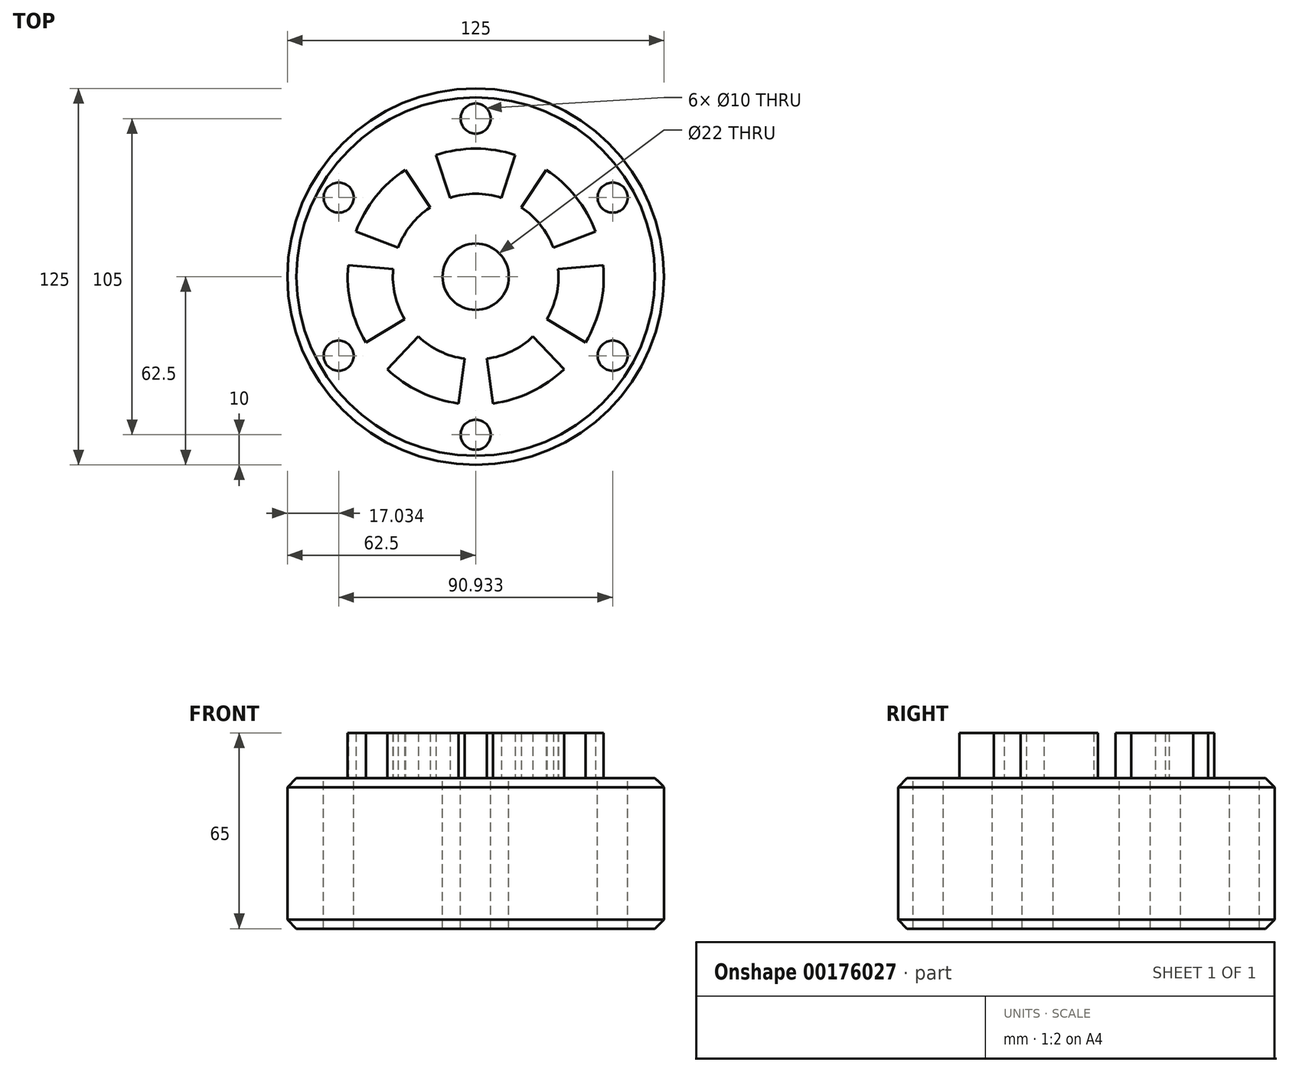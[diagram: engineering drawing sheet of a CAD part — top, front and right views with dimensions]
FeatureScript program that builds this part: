
annotation { "Feature Type Name" : "Feature", "Feature Type Description" : "" }
export const myFeature = defineFeature(function(context is Context, id is Id, definition is map)
    precondition{}
    {
        {
            var Q0;
            Q0=qCreatedBy(makeId("Top.planeOp"),FACE);
            var sketch = newSketch(context, id + "F0", { "sketchPlane" : qUnion([Q0])});
            skCircle(sketch, "E0", {"center": v(0, 0) * mm, "radius": 62.5 * mm});
            skSolve(sketch);
        }
        {
            var Q0;
            Q0=makeQuery(id+"F0.imprint","IMPRINT",FACE,{"disambiguationData":[TD([[makeQuery(id+"F0.imprint","IMPRINT",EDGE,{"derivedFrom":sQuery(id+"F0.wireOp",EDGE,"E0")}),1.0]])]});
            extrude(context, id + "F1", {"entities" : qUnion([Q0]), "depth" : 50 * mm});
        }
        {
            var Q0;
            Q0=makeQuery(id+"F1.opExtrude","CAP_FACE",FACE,{"disambiguationData":[OSD([sQuery(id+"F0.wireOp",EDGE,"E0")])],"isStart":false});
            var sketch = newSketch(context, id + "F2", { "sketchPlane" : qUnion([Q0])});
            skArc(sketch, "E1", {"start": v(8.5, 26.15) * mm, "mid": v(0, 27.5) * mm, "end": v(-8.5, 26.15) * mm});
            skArc(sketch, "E2", {"start": v(13.14, 40.42) * mm, "mid": v(0, 42.5) * mm, "end": v(-13.14, 40.42) * mm});
            skLineSegment(sketch, "E3", {"start": v(-8.5, 26.15) * mm, "end": v(-13.14, 40.42) * mm});
            skLineSegment(sketch, "E4", {"start": v(8.5, 26.15) * mm, "end": v(13.14, 40.42) * mm});
            skLineSegment(sketch, "E5.1.0", {"start": v(-25.75, 9.66) * mm, "end": v(-39.8, 14.93) * mm});
            skArc(sketch, "E5.1.1", {"start": v(-23.41, 35.47) * mm, "mid": v(-33.23, 26.5) * mm, "end": v(-39.8, 14.93) * mm});
            skLineSegment(sketch, "E5.1.2", {"start": v(-15.15, 22.95) * mm, "end": v(-23.41, 35.47) * mm});
            skArc(sketch, "E5.1.3", {"start": v(-15.15, 22.95) * mm, "mid": v(-21.5, 17.15) * mm, "end": v(-25.75, 9.66) * mm});
            skLineSegment(sketch, "E5.2.0", {"start": v(-23.6, -14.1) * mm, "end": v(-36.48, -21.8) * mm});
            skArc(sketch, "E5.2.1", {"start": v(-42.33, 3.81) * mm, "mid": v(-41.43, -9.46) * mm, "end": v(-36.48, -21.8) * mm});
            skLineSegment(sketch, "E5.2.2", {"start": v(-27.39, 2.47) * mm, "end": v(-42.33, 3.81) * mm});
            skArc(sketch, "E5.2.3", {"start": v(-27.39, 2.47) * mm, "mid": v(-26.81, -6.12) * mm, "end": v(-23.6, -14.1) * mm});
            skLineSegment(sketch, "E5.3.0", {"start": v(-3.69, -27.25) * mm, "end": v(-5.7, -42.12) * mm});
            skArc(sketch, "E5.3.1", {"start": v(-29.37, -30.72) * mm, "mid": v(-18.44, -38.3) * mm, "end": v(-5.7, -42.12) * mm});
            skLineSegment(sketch, "E5.3.2", {"start": v(-19, -19.88) * mm, "end": v(-29.37, -30.72) * mm});
            skArc(sketch, "E5.3.3", {"start": v(-19, -19.88) * mm, "mid": v(-11.93, -24.78) * mm, "end": v(-3.69, -27.25) * mm});
            skLineSegment(sketch, "E5.4.0", {"start": v(19, -19.88) * mm, "end": v(29.37, -30.72) * mm});
            skArc(sketch, "E5.4.1", {"start": v(5.7, -42.12) * mm, "mid": v(18.44, -38.3) * mm, "end": v(29.37, -30.72) * mm});
            skLineSegment(sketch, "E5.4.2", {"start": v(3.69, -27.25) * mm, "end": v(5.7, -42.12) * mm});
            skArc(sketch, "E5.4.3", {"start": v(3.69, -27.25) * mm, "mid": v(11.93, -24.78) * mm, "end": v(19, -19.88) * mm});
            skLineSegment(sketch, "E5.5.0", {"start": v(27.39, 2.47) * mm, "end": v(42.33, 3.81) * mm});
            skArc(sketch, "E5.5.1", {"start": v(36.48, -21.8) * mm, "mid": v(41.43, -9.46) * mm, "end": v(42.33, 3.81) * mm});
            skLineSegment(sketch, "E5.5.2", {"start": v(23.6, -14.1) * mm, "end": v(36.48, -21.8) * mm});
            skArc(sketch, "E5.5.3", {"start": v(23.6, -14.1) * mm, "mid": v(26.81, -6.12) * mm, "end": v(27.39, 2.47) * mm});
            skLineSegment(sketch, "E5.6.0", {"start": v(15.15, 22.95) * mm, "end": v(23.41, 35.47) * mm});
            skArc(sketch, "E5.6.1", {"start": v(39.8, 14.93) * mm, "mid": v(33.23, 26.5) * mm, "end": v(23.41, 35.47) * mm});
            skLineSegment(sketch, "E5.6.2", {"start": v(25.75, 9.66) * mm, "end": v(39.8, 14.93) * mm});
            skArc(sketch, "E5.6.3", {"start": v(25.75, 9.66) * mm, "mid": v(21.5, 17.15) * mm, "end": v(15.15, 22.95) * mm});
            skSolve(sketch);
        }
        {
            var Q0;
            Q0 = qSketchRegion(id + "F2", true);
            extrude(context, id + "F3", {"entities" : qUnion([Q0]), "operationType" : NewBodyOperationType.ADD, "depth" : 15 * mm});
        }
        {
            var Q0;
            Q0=makeQuery(id+"F1.opExtrude","CAP_FACE",FACE,{"disambiguationData":[OSD([sQuery(id+"F0.wireOp",EDGE,"E0")])],"isStart":false});
            var sketch = newSketch(context, id + "F4", { "sketchPlane" : qUnion([Q0])});
            skCircle(sketch, "E6", {"center": v(0, 0) * mm, "radius": 11 * mm});
            skSolve(sketch);
        }
        {
            var Q0;
            Q0 = qSketchRegion(id + "F4", true);
            extrude(context, id + "F5", {"entities" : qUnion([Q0]), "operationType" : NewBodyOperationType.REMOVE, "endBound" : BoundingType.THROUGH_ALL, "oppositeDirection" : true, "depth" : 25 * mm});
        }
        {
            var Q0;
            Q0=makeQuery(id+"F1.opExtrude","CAP_FACE",FACE,{"disambiguationData":[OSD([sQuery(id+"F0.wireOp",EDGE,"E0")])],"isStart":false});
            var sketch = newSketch(context, id + "F6", { "sketchPlane" : qUnion([Q0])});
            skArc(sketch, "E7", {"start": v(-42.76, 30.46) * mm, "mid": v(-44.16, 28.39) * mm, "end": v(-45.47, 26.25) * mm});
            skCircle(sketch, "E8", {"center": v(0, 52.5) * mm, "radius": 5 * mm});
            skCircle(sketch, "E9.1.0", {"center": v(-45.47, 26.25) * mm, "radius": 5 * mm});
            skArc(sketch, "E9.1.1", {"start": v(-42.76, 30.46) * mm, "mid": v(-45.47, 26.25) * mm, "end": v(-47.76, 21.8) * mm});
            skCircle(sketch, "E9.2.0", {"center": v(-45.47, -26.25) * mm, "radius": 5 * mm});
            skCircle(sketch, "E9.3.0", {"center": v(0, -52.5) * mm, "radius": 5 * mm});
            skArc(sketch, "E9.3.1", {"start": v(-42.76, 30.46) * mm, "mid": v(-45.47, 26.25) * mm, "end": v(-47.76, 21.8) * mm});
            skCircle(sketch, "E9.4.0", {"center": v(45.47, -26.25) * mm, "radius": 5 * mm});
            skArc(sketch, "E9.4.1", {"start": v(-42.76, 30.46) * mm, "mid": v(-45.47, 26.25) * mm, "end": v(-47.76, 21.8) * mm});
            skCircle(sketch, "E9.5.0", {"center": v(45.47, 26.25) * mm, "radius": 5 * mm});
            skArc(sketch, "E9.5.1", {"start": v(-42.76, 30.46) * mm, "mid": v(-45.47, 26.25) * mm, "end": v(-47.76, 21.8) * mm});
            skArc(sketch, "E10.trimOffspring", {"start": v(5, 52.26) * mm, "mid": v(0, 52.5) * mm, "end": v(-5, 52.26) * mm});
            skArc(sketch, "E11.trimOffspring", {"start": v(47.76, 21.8) * mm, "mid": v(45.47, 26.25) * mm, "end": v(42.76, 30.46) * mm});
            skArc(sketch, "E12.trimOffspring", {"start": v(47.76, 21.8) * mm, "mid": v(46.66, 24.06) * mm, "end": v(45.47, 26.25) * mm});
            skArc(sketch, "E13.trimOffspring", {"start": v(42.76, -30.46) * mm, "mid": v(45.47, -26.25) * mm, "end": v(47.76, -21.8) * mm});
            skArc(sketch, "E14.trimOffspring", {"start": v(-5, -52.26) * mm, "mid": v(0, -52.5) * mm, "end": v(5, -52.26) * mm});
            skArc(sketch, "E15.trimOffspring", {"start": v(-5, -52.26) * mm, "mid": v(-2.5, -52.44) * mm, "end": v(0, -52.5) * mm});
            skArc(sketch, "E16.trimOffspring", {"start": v(-47.76, -21.8) * mm, "mid": v(-45.47, -26.25) * mm, "end": v(-42.76, -30.46) * mm});
            skArc(sketch, "E17.trimOffspring", {"start": v(-47.76, -21.8) * mm, "mid": v(-46.66, -24.06) * mm, "end": v(-45.47, -26.25) * mm});
            skSolve(sketch);
        }
        {
            var Q0;
            Q0 = qSketchRegion(id + "F6", true);
            extrude(context, id + "F7", {"entities" : qUnion([Q0]), "operationType" : NewBodyOperationType.REMOVE, "endBound" : BoundingType.THROUGH_ALL, "oppositeDirection" : true, "depth" : 25 * mm});
        }
        {
            var Q0;
            Q0=makeQuery(id+"F1.opExtrude","CAP_EDGE",EDGE,{"disambiguationData":[OSD([sQuery(id+"F0.wireOp",EDGE,"E0")])],"isStart":false});
            var Q1;
            Q1=makeQuery(id+"F1.opExtrude","CAP_EDGE",EDGE,{"disambiguationData":[OSD([sQuery(id+"F0.wireOp",EDGE,"E0")])],"isStart":true});
            chamfer(context, id + "F8", {"entities" : qUnion([Q0, Q1]), "width" : 3 * mm, "tangentPropagation" : true});
        }
    });
